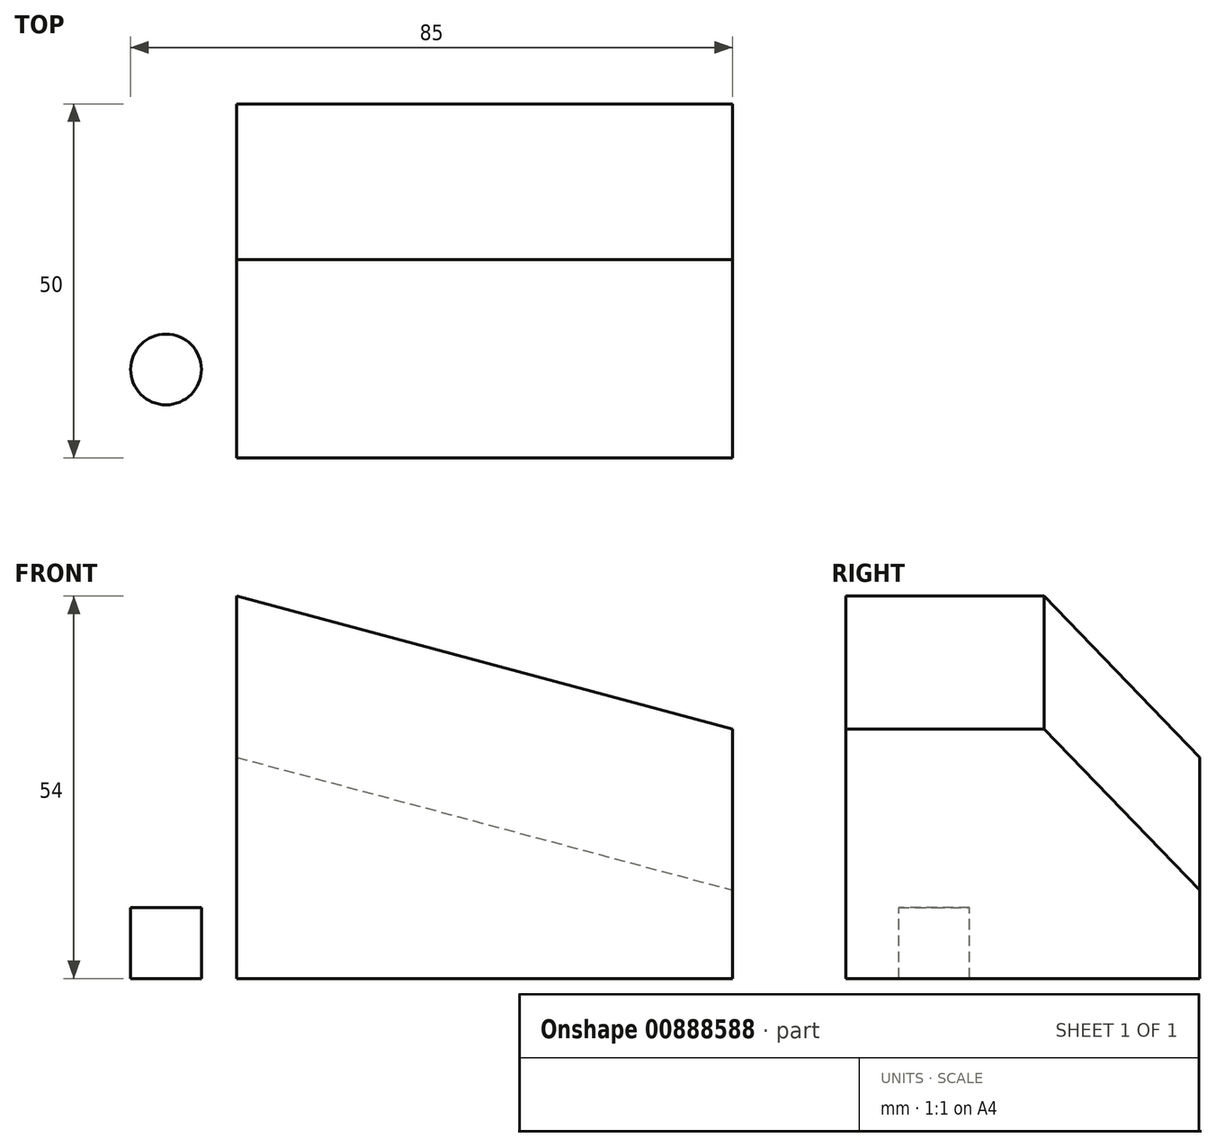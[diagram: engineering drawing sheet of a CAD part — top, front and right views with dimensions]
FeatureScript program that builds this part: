
annotation { "Feature Type Name" : "Feature", "Feature Type Description" : "" }
export const myFeature = defineFeature(function(context is Context, id is Id, definition is map)
    precondition{}
    {
        {
            var Q0;
            Q0=qCreatedBy(makeId("Top.planeOp"),FACE);
            var sketch = newSketch(context, id + "F0", { "sketchPlane" : qUnion([Q0])});
            skLineSegment(sketch, "E0.bottom", {"start": v(45, -25) * mm, "end": v(-45, -25) * mm});
            skLineSegment(sketch, "E0.top", {"start": v(45, 25) * mm, "end": v(-45, 25) * mm});
            skLineSegment(sketch, "E0.left", {"start": v(45, -25) * mm, "end": v(45, 25) * mm});
            skLineSegment(sketch, "E0.right", {"start": v(-45, -25) * mm, "end": v(-45, 25) * mm});
            skPoint(sketch, "E0.middle", {"position": v(0, 0) * mm});
            skSolve(sketch);
        }
        {
            var Q0;
            Q0=makeQuery(id+"F0.imprint","IMPRINT",FACE,{"disambiguationData":[TD([[makeQuery(id+"F0.imprint","IMPRINT",EDGE,{"derivedFrom":sQuery(id+"F0.wireOp",EDGE,"E0.bottom")}),-1.0]])]});
            extrude(context, id + "F1", {"entities" : qUnion([Q0]), "depth" : 54 * mm, "offsetDistance" : 25 * mm});
        }
        {
            var Q0;
            Q0=makeQuery(id+"F1.opExtrude","SWEPT_FACE",FACE,{"disambiguationData":[OSD([sQuery(id+"F0.wireOp",EDGE,"E0.bottom")])]});
            var sketch = newSketch(context, id + "F2", { "sketchPlane" : qUnion([Q0])});
            skLineSegment(sketch, "E1", {"start": v(-25, 54) * mm, "end": v(76.9, 26.7) * mm});
            skLineSegment(sketch, "E2", {"start": v(-45, 10) * mm, "end": v(-25, 10) * mm});
            skLineSegment(sketch, "E3", {"start": v(-25, 10) * mm, "end": v(-25, 54) * mm});
            skSolve(sketch);
        }
        {
            var Q0;
            {var subQ0=sQuery(id+"F2.wireOp",EDGE,"E2");Q0=makeQuery(id+"F2.imprint","IMPRINT",FACE,{"disambiguationData":[TD([[makeQuery(id+"F2.imprint","IMPRINT",EDGE,{"derivedFrom":subQ0}),1.0]])]});}
            var Q1;
            {var subQ0=sQuery(id+"F2.wireOp",EDGE,"E1");var subQ1=sQuery(id+"F0.wireOp",EDGE,"E0.bottom");var subQ2=makeQuery(id+"F1.opExtrude","CAP_EDGE",EDGE,{"disambiguationData":[OSD([subQ1])],"isStart":false});var subQ3=makeQuery(id+"F2.imprint","INTERSECT",VERTEX,{"derivedFrom":[subQ2,subQ0,sQuery(id+"F2.wireOp",EDGE,"E3")]});Q1=makeQuery(id+"F2.imprint","IMPRINT",FACE,{"disambiguationData":[TD([[makeQuery(id+"F2.imprint","IMPRINT",EDGE,{"disambiguationData":[TD([[subQ3,-1.0]])],"derivedFrom":subQ0}),1.0]])]});}
            extrude(context, id + "F3", {"entities" : qUnion([Q0, Q1]), "operationType" : NewBodyOperationType.REMOVE, "endBound" : BoundingType.THROUGH_ALL, "oppositeDirection" : true, "depth" : 25 * mm, "offsetDistance" : 25 * mm});
        }
        {
            var Q0;
            Q0=makeQuery(id+"F3.boolean.opBoolean","COPY",EDGE,{"derivedFrom":makeQuery(id+"F3.opExtrude","CAP_EDGE",EDGE,{"disambiguationData":[OSD([sQuery(id+"F2.wireOp",EDGE,"E1")])],"isStart":true})});
            var Q1;
            Q1=makeQuery(id+"F3.boolean.opBoolean","INTERSECT",EDGE,{"derivedFrom":[makeQuery(id+"F1.opExtrude","SWEPT_FACE",FACE,{"disambiguationData":[OSD([sQuery(id+"F0.wireOp",EDGE,"E0.top")])]}),makeQuery(id+"F3.opExtrude","SWEPT_FACE",FACE,{"disambiguationData":[OSD([sQuery(id+"F2.wireOp",EDGE,"E1")])]})]});
            chamfer(context, id + "F4", {"entities" : qUnion([Q0, Q1]), "width" : 22 * mm, "tangentPropagation" : true});
        }
        {
            var Q0;
            Q0=makeQuery(id+"F1.opExtrude","SWEPT_FACE",FACE,{"disambiguationData":[OSD([sQuery(id+"F0.wireOp",EDGE,"E0.bottom")])]});
            var sketch = newSketch(context, id + "F5", { "sketchPlane" : qUnion([Q0])});
            skLineSegment(sketch, "E4", {"start": v(45, 11.33) * mm, "end": v(45, 56.2) * mm, "construction": true});
            skLineSegment(sketch, "E5.0", {"start": v(18, 11.33) * mm, "end": v(18, 56.2) * mm, "construction": true});
            skLineSegment(sketch, "E6", {"start": v(18, 42.58) * mm, "end": v(61, 17.75) * mm});
            skLineSegment(sketch, "E7", {"start": v(18, 42.58) * mm, "end": v(61.42, 42.58) * mm});
            skLineSegment(sketch, "E8", {"start": v(61.42, 42.58) * mm, "end": v(61, 17.75) * mm});
            skSolve(sketch);
        }
        {
            var Q0;
            Q0=makeQuery(id+"F5.imprint","IMPRINT",FACE,{"disambiguationData":[TD([[makeQuery(id+"F5.imprint","IMPRINT",EDGE,{"derivedFrom":sQuery(id+"F5.wireOp",EDGE,"E6")}),1.0]])]});
            extrude(context, id + "F6", {"entities" : qUnion([Q0]), "operationType" : NewBodyOperationType.REMOVE, "endBound" : BoundingType.THROUGH_ALL, "oppositeDirection" : true, "depth" : 25 * mm, "offsetDistance" : 25 * mm});
        }
        {
            var Q0;
            Q0=makeQuery(id+"F3.boolean.opBoolean","COPY",FACE,{"derivedFrom":makeQuery(id+"F3.opExtrude","SWEPT_FACE",FACE,{"disambiguationData":[OSD([sQuery(id+"F2.wireOp",EDGE,"E2")])]})});
            var sketch = newSketch(context, id + "F7", { "sketchPlane" : qUnion([Q0])});
            skLineSegment(sketch, "E9", {"start": v(-35, 25) * mm, "end": v(-35, 0) * mm, "construction": true});
            skLineSegment(sketch, "E10", {"start": v(-22.72, 0) * mm, "end": v(-53.1, 0) * mm, "construction": true});
            skPoint(sketch, "E10.startSnap0", {"position": v(-25, 0) * mm});
            skPoint(sketch, "E11.orphan", {"position": v(-35, -25) * mm});
            skCircle(sketch, "E12", {"center": v(-35, 12.5) * mm, "radius": 5 * mm});
            skCircle(sketch, "E13.MirrorC", {"center": v(-35, -12.5) * mm, "radius": 5 * mm});
            skLineSegment(sketch, "E14.MirrorCS", {"start": v(-35, -25) * mm, "end": v(-35, 0) * mm, "construction": true});
            skSolve(sketch);
        }
        {
            var Q0;
            Q0=makeQuery(id+"F7.imprint","IMPRINT",FACE,{"disambiguationData":[TD([[makeQuery(id+"F7.imprint","IMPRINT",EDGE,{"derivedFrom":sQuery(id+"F7.wireOp",EDGE,"E12")}),1.0]])]});
            var Q1;
            Q1=makeQuery(id+"F7.imprint","IMPRINT",FACE,{"disambiguationData":[TD([[makeQuery(id+"F7.imprint","IMPRINT",EDGE,{"derivedFrom":sQuery(id+"F7.wireOp",EDGE,"E13.MirrorC")}),-1.0]])]});
            extrude(context, id + "F8", {"entities" : qUnion([Q0, Q1]), "operationType" : NewBodyOperationType.REMOVE, "oppositeDirection" : true, "depth" : 25 * mm, "offsetDistance" : 25 * mm});
        }
    });
